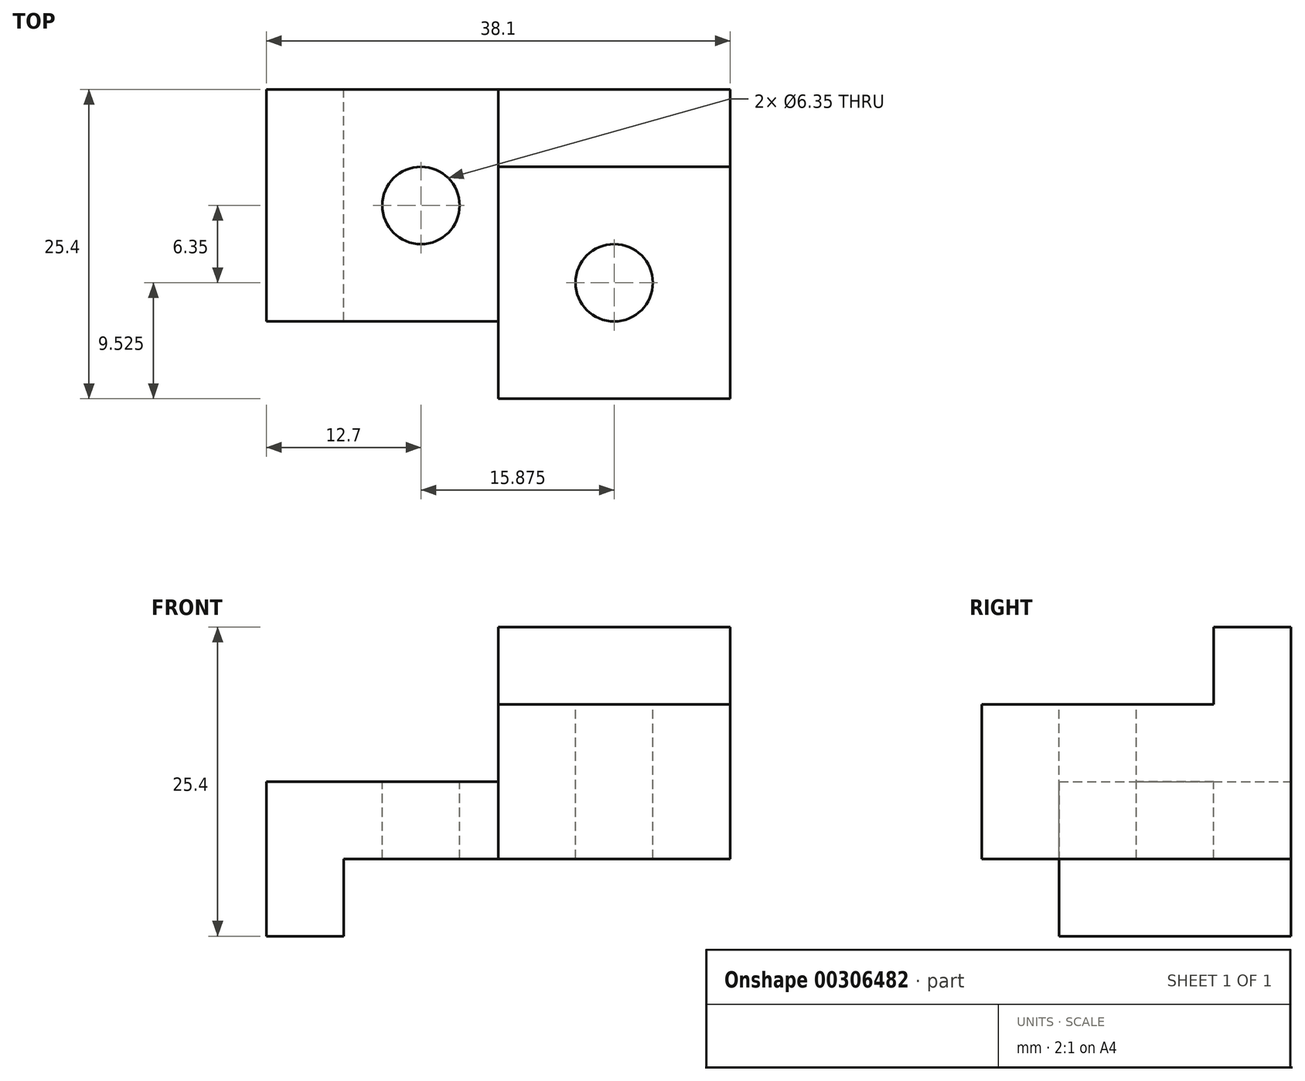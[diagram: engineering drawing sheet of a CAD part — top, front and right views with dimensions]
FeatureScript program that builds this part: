
annotation { "Feature Type Name" : "Feature", "Feature Type Description" : "" }
export const myFeature = defineFeature(function(context is Context, id is Id, definition is map)
    precondition{}
    {
        {
            var Q0;
            Q0=qCreatedBy(makeId("Front.planeOp"),FACE);
            var sketch = newSketch(context, id + "F0", { "sketchPlane" : qUnion([Q0])});
            skLineSegment(sketch, "E0", {"start": v(0, 0) * mm, "end": v(0, 12.7) * mm});
            skLineSegment(sketch, "E1", {"start": v(0, 12.7) * mm, "end": v(19.05, 12.7) * mm});
            skLineSegment(sketch, "E2", {"start": v(19.05, 12.7) * mm, "end": v(19.05, 25.4) * mm});
            skLineSegment(sketch, "E3", {"start": v(19.05, 25.4) * mm, "end": v(38.1, 25.4) * mm});
            skLineSegment(sketch, "E4", {"start": v(0, 0) * mm, "end": v(6.35, 0) * mm});
            skLineSegment(sketch, "E5", {"start": v(6.35, 0) * mm, "end": v(6.35, 6.35) * mm});
            skLineSegment(sketch, "E6", {"start": v(6.35, 6.35) * mm, "end": v(38.1, 6.35) * mm});
            skLineSegment(sketch, "E7", {"start": v(38.1, 6.35) * mm, "end": v(38.1, 25.4) * mm});
            skLineSegment(sketch, "E8", {"start": v(19.05, 12.7) * mm, "end": v(19.05, 6.35) * mm});
            skLineSegment(sketch, "E9", {"start": v(19.05, 19.05) * mm, "end": v(38.1, 19.05) * mm});
            skSolve(sketch);
        }
        {
            var Q0;
            {var subQ0=sQuery(id+"F0.wireOp",EDGE,"E3");Q0=makeQuery(id+"F0.imprint","IMPRINT",FACE,{"disambiguationData":[TD([[makeQuery(id+"F0.imprint","IMPRINT",EDGE,{"derivedFrom":subQ0}),-1.0]])]});}
            extrude(context, id + "F1", {"entities" : qUnion([Q0]), "depth" : 6.35 * mm});
        }
        {
            var Q0;
            {var subQ0=sQuery(id+"F0.wireOp",EDGE,"E8");Q0=makeQuery(id+"F0.imprint","IMPRINT",FACE,{"disambiguationData":[TD([[makeQuery(id+"F0.imprint","IMPRINT",EDGE,{"derivedFrom":subQ0}),1.0]])]});}
            extrude(context, id + "F2", {"entities" : qUnion([Q0]), "operationType" : NewBodyOperationType.ADD, "depth" : 25.4 * mm});
        }
        {
            var Q0;
            Q0=makeQuery(id+"F0.imprint","IMPRINT",FACE,{"disambiguationData":[TD([[makeQuery(id+"F0.imprint","IMPRINT",EDGE,{"derivedFrom":sQuery(id+"F0.wireOp",EDGE,"E0")}),-1.0]])]});
            extrude(context, id + "F3", {"entities" : qUnion([Q0]), "operationType" : NewBodyOperationType.ADD, "depth" : 19.05 * mm});
        }
        {
            var Q0;
            Q0=makeQuery(id+"F2.opExtrude","SWEPT_FACE",FACE,{"disambiguationData":[OSD([sQuery(id+"F0.wireOp",EDGE,"E9")])]});
            var sketch = newSketch(context, id + "F4", { "sketchPlane" : qUnion([Q0])});
            skCircle(sketch, "E10", {"center": v(28.58, -15.88) * mm, "radius": 3.17 * mm});
            skCircle(sketch, "E11", {"center": v(12.7, -9.53) * mm, "radius": 3.18 * mm});
            skSolve(sketch);
        }
        {
            var Q0;
            Q0 = qSketchRegion(id + "F4", true);
            extrude(context, id + "F5", {"entities" : qUnion([Q0]), "operationType" : NewBodyOperationType.REMOVE, "endBound" : BoundingType.THROUGH_ALL, "oppositeDirection" : true, "depth" : 25.4 * mm});
        }
    });
